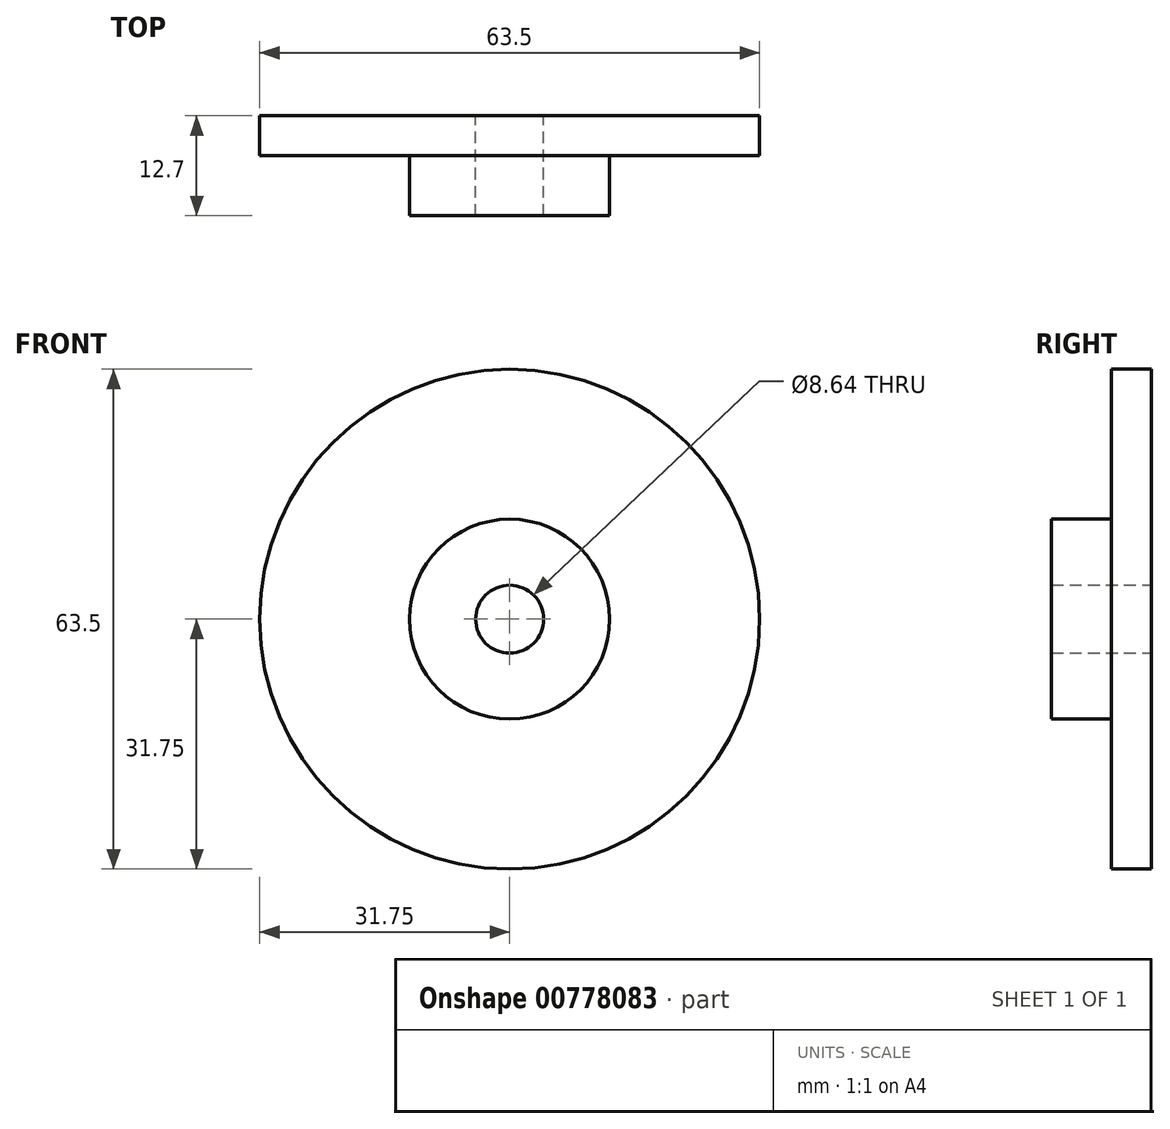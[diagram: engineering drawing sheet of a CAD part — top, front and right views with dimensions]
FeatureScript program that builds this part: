
annotation { "Feature Type Name" : "Feature", "Feature Type Description" : "" }
export const myFeature = defineFeature(function(context is Context, id is Id, definition is map)
    precondition{}
    {
        {
            var Q0;
            Q0=qCreatedBy(makeId("Front.planeOp"),FACE);
            var sketch = newSketch(context, id + "F0", { "sketchPlane" : qUnion([Q0])});
            skCircle(sketch, "E0", {"center": v(0, 0) * mm, "radius": 12.7 * mm});
            skSolve(sketch);
        }
        {
            var Q0;
            Q0=qSketchRegion(id+"F0",true);
            extrude(context, id + "F1", {"entities" : qUnion([Q0]), "depth" : 12.7 * mm, "offsetDistance" : 25.4 * mm});
        }
        {
            var Q0;
            Q0=qCreatedBy(makeId("Front.planeOp"),FACE);
            var sketch = newSketch(context, id + "F2", { "sketchPlane" : qUnion([Q0])});
            skCircle(sketch, "E1", {"center": v(0, 0) * mm, "radius": 31.75 * mm});
            skSolve(sketch);
        }
        {
            var Q0;
            Q0 = qSketchRegion(id + "F2", true);
            extrude(context, id + "F3", {"entities" : qUnion([Q0]), "operationType" : NewBodyOperationType.ADD, "depth" : 5.08 * mm, "offsetDistance" : 25.4 * mm});
        }
        {
            var Q0;
            Q0=qCreatedBy(makeId("Front.planeOp"),FACE);
            var sketch = newSketch(context, id + "F4", { "sketchPlane" : qUnion([Q0])});
            skCircle(sketch, "E2", {"center": v(0, 0) * mm, "radius": 4.32 * mm});
            skSolve(sketch);
        }
        {
            var Q0;
            Q0 = qSketchRegion(id + "F4", true);
            extrude(context, id + "F5", {"entities" : qUnion([Q0]), "operationType" : NewBodyOperationType.REMOVE, "endBound" : BoundingType.THROUGH_ALL, "depth" : 25.4 * mm, "offsetDistance" : 25.4 * mm, "hasSecondDirection" : true, "secondDirectionBound" : SecondDirectionBoundingType.THROUGH_ALL, "secondDirectionOppositeDirection" : true, "secondDirectionDepth" : 25.4 * mm});
        }
    });
